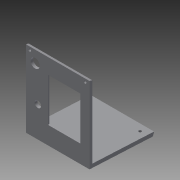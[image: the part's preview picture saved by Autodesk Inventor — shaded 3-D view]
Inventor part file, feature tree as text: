
AUTODESK INVENTOR PART (.ipt)
format: ipt  version: 2015 SP2 (Build 190223200, 223)  size: 173,056 bytes
history: native  units: mm
features: extrude x7, projected_geometry x7, sketch x6, hole x2, plane x1
ambient origin geometry x8: Origin, YZ Plane, XZ Plane, XY Plane, X Axis, Y Axis, Z Axis, Center Point
bodies: Volumenkörper1 (feature_tree)
feature tree (23):
  extrude  "Extrusion1"  Depth=78.309mm
  plane  "Arbeitsebene1"
  extrude  "Extrusion2"  [1 undecoded]
  hole  "Bohrung1"  [1 undecoded]
  sketch  "Skizze5"  dims[d7=4.0mm d8=0.0mm d12=7.634mm]
  extrude  "Extrusion4"  Depth=4.0mm
  extrude  "Extrusion5"  Depth=7.634mm
  hole  "Bohrung2"  [1 undecoded]
  extrude  "Extrusion6"  Depth=47.0mm
  sketch  "Skizze7"  dims[d16=7.5mm d17=3.0mm d18=6.0mm d19=4.0mm d20=2.0mm d21=90.0deg d22=8.0mm d23=20.594885mm d24=35.1mm d25=47.0mm d26=54.0mm d27=46.0mm d28=5.0mm d29=3.5mm d30=12.4mm d31=5.0mm d32=7.0mm d34=13.0mm d35=10.0mm d37=10.0mm d40=5.0mm d41=2.588mm d42=4.0mm d43=69.0mm d44=0.0mm d45=1.5mm d46=0.0mm d47=3.0mm d48=6.0mm d49=4.0mm d50=2.0mm d51=90.0deg d52=8.0mm d53=20.594885mm d54=69.0mm d55=0.0mm d56=29.3mm d57=12.0mm d59=15.0deg d60=80.0mm d61=0.0mm d62=15.0deg d63=69.0mm d64=0.0mm]
  extrude  "Extrusion7"  Depth=54.0mm
  extrude  "Extrusion8"  Depth=46.0mm
  sketch  "Skizze1"  dims[d0=69.0mm d1=78.309mm]
  sketch  "Skizze2"  dims[d2=3.0mm d3=0.0mm d4=-16.207127mm]
  projected_geometry  "Projizierte Kontur1"
  sketch  "Skizze4"  dims[d5=69.0mm d6=67.1mm]
  projected_geometry  "Projizierte Kontur4"
  projected_geometry  "Projizierte Kontur5"
  projected_geometry  "Projizierte Kontur6"
  sketch  "Skizze6"  dims[d14=7.5mm d15=7.634mm]
  projected_geometry  "Projizierte Kontur7"
  projected_geometry  "Projizierte Kontur8"
  projected_geometry  "Projizierte Kontur9"
note: 3 required parameter values undecoded (feature->parameter linkage not recoverable at this tier; creation-order binding heuristic only, values carry confidence <= 0.55)
